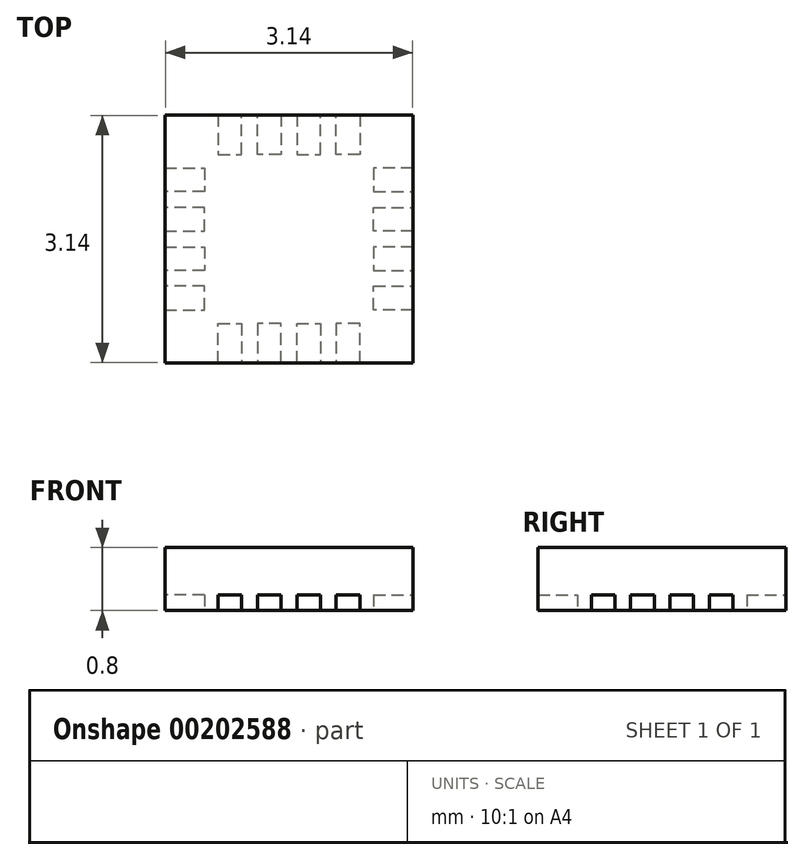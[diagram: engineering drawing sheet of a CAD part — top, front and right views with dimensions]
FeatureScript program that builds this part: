
annotation { "Feature Type Name" : "Feature", "Feature Type Description" : "" }
export const myFeature = defineFeature(function(context is Context, id is Id, definition is map)
    precondition{}
    {
        {
            var Q0;
            Q0=qCreatedBy(makeId("Top.planeOp"),FACE);
            var sketch = newSketch(context, id + "F0", { "sketchPlane" : qUnion([Q0])});
            skLineSegment(sketch, "E0.bottom", {"start": v(1.57, 1.57) * mm, "end": v(-1.58, 1.57) * mm});
            skLineSegment(sketch, "E0.top", {"start": v(1.57, -1.57) * mm, "end": v(-1.58, -1.57) * mm});
            skLineSegment(sketch, "E0.left", {"start": v(1.57, 1.58) * mm, "end": v(1.57, -1.57) * mm});
            skLineSegment(sketch, "E0.right", {"start": v(-1.58, 1.57) * mm, "end": v(-1.58, -1.57) * mm});
            skPoint(sketch, "E0.middle", {"position": v(0, 0) * mm});
            skSolve(sketch);
        }
        {
            var Q0;
            Q0 = qSketchRegion(id + "F0", true);
            extrude(context, id + "F1", {"entities" : qUnion([Q0]), "depth" : 0.8 * mm});
        }
        {
            var Q0;
            Q0=makeQuery(id+"F1.opExtrude","CAP_FACE",FACE,{"disambiguationData":[OSD([sQuery(id+"F0.wireOp",EDGE,"E0.bottom"),sQuery(id+"F0.wireOp",EDGE,"E0.top"),sQuery(id+"F0.wireOp",EDGE,"E0.left"),sQuery(id+"F0.wireOp",EDGE,"E0.right")])],"isStart":true});
            var sketch = newSketch(context, id + "F2", { "sketchPlane" : qUnion([Q0])});
            skLineSegment(sketch, "E1", {"start": v(0, 0) * mm, "end": v(0, 1.57) * mm, "construction": true});
            skPoint(sketch, "E2", {"position": v(0.25, 1.57) * mm});
            skLineSegment(sketch, "E3", {"start": v(0.1, 1.57) * mm, "end": v(0.4, 1.57) * mm});
            skLineSegment(sketch, "E4", {"start": v(0.1, 1.57) * mm, "end": v(0.1, 1.07) * mm});
            skLineSegment(sketch, "E5", {"start": v(0.1, 1.07) * mm, "end": v(0.4, 1.07) * mm});
            skLineSegment(sketch, "E6", {"start": v(0.4, 1.07) * mm, "end": v(0.4, 1.57) * mm});
            skPoint(sketch, "E7.MirrorP", {"position": v(0.75, 1.58) * mm});
            skLineSegment(sketch, "E8.MirrorCS", {"start": v(0.9, 1.58) * mm, "end": v(0.6, 1.58) * mm});
            skLineSegment(sketch, "E9.MirrorCS", {"start": v(0.9, 1.58) * mm, "end": v(0.9, 1.08) * mm});
            skLineSegment(sketch, "E10.MirrorCS", {"start": v(0.6, 1.08) * mm, "end": v(0.6, 1.58) * mm});
            skLineSegment(sketch, "E11.MirrorCS", {"start": v(0.9, 1.08) * mm, "end": v(0.6, 1.08) * mm});
            skLineSegment(sketch, "E12.MirrorCS", {"start": v(-0.1, 1.57) * mm, "end": v(-0.4, 1.57) * mm});
            skPoint(sketch, "E13.MirrorP", {"position": v(-0.25, 1.57) * mm});
            skLineSegment(sketch, "E14.MirrorCS", {"start": v(-0.1, 1.57) * mm, "end": v(-0.1, 1.07) * mm});
            skPoint(sketch, "E15.MirrorP", {"position": v(-0.75, 1.58) * mm});
            skLineSegment(sketch, "E16.MirrorCS", {"start": v(-0.1, 1.07) * mm, "end": v(-0.4, 1.07) * mm});
            skLineSegment(sketch, "E17.MirrorCS", {"start": v(-0.4, 1.07) * mm, "end": v(-0.4, 1.57) * mm});
            skLineSegment(sketch, "E18.MirrorCS", {"start": v(-0.9, 1.58) * mm, "end": v(-0.6, 1.58) * mm});
            skLineSegment(sketch, "E19.MirrorCS", {"start": v(-0.9, 1.57) * mm, "end": v(-0.9, 1.07) * mm});
            skLineSegment(sketch, "E20.MirrorCS", {"start": v(-0.6, 1.08) * mm, "end": v(-0.6, 1.58) * mm});
            skLineSegment(sketch, "E21.MirrorCS", {"start": v(-0.9, 1.08) * mm, "end": v(-0.6, 1.08) * mm});
            skPoint(sketch, "E22.1.0", {"position": v(-1.58, -0.75) * mm});
            skLineSegment(sketch, "E22.1.1", {"start": v(-1.57, 0.1) * mm, "end": v(-1.57, 0.4) * mm});
            skLineSegment(sketch, "E22.1.2", {"start": v(-1.08, 0.6) * mm, "end": v(-1.58, 0.6) * mm});
            skLineSegment(sketch, "E22.1.3", {"start": v(-1.58, -0.9) * mm, "end": v(-1.58, -0.6) * mm});
            skLineSegment(sketch, "E22.1.4", {"start": v(-1.58, 0.9) * mm, "end": v(-1.08, 0.9) * mm});
            skLineSegment(sketch, "E22.1.5", {"start": v(-1.58, 0.9) * mm, "end": v(-1.58, 0.6) * mm});
            skLineSegment(sketch, "E22.1.6", {"start": v(-1.08, 0.9) * mm, "end": v(-1.08, 0.6) * mm});
            skPoint(sketch, "E22.1.7", {"position": v(-1.58, 0.75) * mm});
            skLineSegment(sketch, "E22.1.8", {"start": v(-1.07, 0.4) * mm, "end": v(-1.57, 0.4) * mm});
            skLineSegment(sketch, "E22.1.9", {"start": v(-1.07, 0.1) * mm, "end": v(-1.07, 0.4) * mm});
            skLineSegment(sketch, "E22.1.10", {"start": v(-1.57, -0.9) * mm, "end": v(-1.07, -0.9) * mm});
            skLineSegment(sketch, "E22.1.11", {"start": v(-1.57, 0.1) * mm, "end": v(-1.07, 0.1) * mm});
            skPoint(sketch, "E22.1.12", {"position": v(-1.57, 0.25) * mm});
            skPoint(sketch, "E22.1.13", {"position": v(-1.57, -0.25) * mm});
            skLineSegment(sketch, "E22.1.14", {"start": v(-1.08, -0.9) * mm, "end": v(-1.08, -0.6) * mm});
            skLineSegment(sketch, "E22.1.15", {"start": v(-1.07, -0.4) * mm, "end": v(-1.57, -0.4) * mm});
            skLineSegment(sketch, "E22.1.16", {"start": v(-1.08, -0.6) * mm, "end": v(-1.58, -0.6) * mm});
            skLineSegment(sketch, "E22.1.17", {"start": v(-1.07, -0.1) * mm, "end": v(-1.07, -0.4) * mm});
            skLineSegment(sketch, "E22.1.18", {"start": v(-1.57, -0.1) * mm, "end": v(-1.07, -0.1) * mm});
            skLineSegment(sketch, "E22.1.19", {"start": v(-1.57, -0.1) * mm, "end": v(-1.57, -0.4) * mm});
            skPoint(sketch, "E22.2.0", {"position": v(0.75, -1.58) * mm});
            skLineSegment(sketch, "E22.2.1", {"start": v(-0.1, -1.57) * mm, "end": v(-0.4, -1.57) * mm});
            skLineSegment(sketch, "E22.2.2", {"start": v(-0.6, -1.08) * mm, "end": v(-0.6, -1.58) * mm});
            skLineSegment(sketch, "E22.2.3", {"start": v(0.9, -1.58) * mm, "end": v(0.6, -1.58) * mm});
            skLineSegment(sketch, "E22.2.4", {"start": v(-0.9, -1.57) * mm, "end": v(-0.9, -1.07) * mm});
            skLineSegment(sketch, "E22.2.5", {"start": v(-0.9, -1.58) * mm, "end": v(-0.6, -1.58) * mm});
            skLineSegment(sketch, "E22.2.6", {"start": v(-0.9, -1.08) * mm, "end": v(-0.6, -1.08) * mm});
            skPoint(sketch, "E22.2.7", {"position": v(-0.75, -1.58) * mm});
            skLineSegment(sketch, "E22.2.8", {"start": v(-0.4, -1.07) * mm, "end": v(-0.4, -1.57) * mm});
            skLineSegment(sketch, "E22.2.9", {"start": v(-0.1, -1.07) * mm, "end": v(-0.4, -1.07) * mm});
            skLineSegment(sketch, "E22.2.10", {"start": v(0.9, -1.58) * mm, "end": v(0.9, -1.08) * mm});
            skLineSegment(sketch, "E22.2.11", {"start": v(-0.1, -1.57) * mm, "end": v(-0.1, -1.07) * mm});
            skPoint(sketch, "E22.2.12", {"position": v(-0.25, -1.57) * mm});
            skPoint(sketch, "E22.2.13", {"position": v(0.25, -1.57) * mm});
            skLineSegment(sketch, "E22.2.14", {"start": v(0.9, -1.08) * mm, "end": v(0.6, -1.08) * mm});
            skLineSegment(sketch, "E22.2.15", {"start": v(0.4, -1.07) * mm, "end": v(0.4, -1.57) * mm});
            skLineSegment(sketch, "E22.2.16", {"start": v(0.6, -1.08) * mm, "end": v(0.6, -1.58) * mm});
            skLineSegment(sketch, "E22.2.17", {"start": v(0.1, -1.07) * mm, "end": v(0.4, -1.07) * mm});
            skLineSegment(sketch, "E22.2.18", {"start": v(0.1, -1.57) * mm, "end": v(0.1, -1.07) * mm});
            skLineSegment(sketch, "E22.2.19", {"start": v(0.1, -1.57) * mm, "end": v(0.4, -1.57) * mm});
            skPoint(sketch, "E22.3.0", {"position": v(1.58, 0.75) * mm});
            skLineSegment(sketch, "E22.3.1", {"start": v(1.57, -0.1) * mm, "end": v(1.57, -0.4) * mm});
            skLineSegment(sketch, "E22.3.2", {"start": v(1.07, -0.6) * mm, "end": v(1.57, -0.6) * mm});
            skLineSegment(sketch, "E22.3.3", {"start": v(1.58, 0.9) * mm, "end": v(1.58, 0.6) * mm});
            skLineSegment(sketch, "E22.3.4", {"start": v(1.57, -0.9) * mm, "end": v(1.07, -0.9) * mm});
            skLineSegment(sketch, "E22.3.5", {"start": v(1.57, -0.9) * mm, "end": v(1.57, -0.6) * mm});
            skLineSegment(sketch, "E22.3.6", {"start": v(1.07, -0.9) * mm, "end": v(1.07, -0.6) * mm});
            skPoint(sketch, "E22.3.7", {"position": v(1.57, -0.75) * mm});
            skLineSegment(sketch, "E22.3.8", {"start": v(1.07, -0.4) * mm, "end": v(1.57, -0.4) * mm});
            skLineSegment(sketch, "E22.3.9", {"start": v(1.07, -0.1) * mm, "end": v(1.07, -0.4) * mm});
            skLineSegment(sketch, "E22.3.10", {"start": v(1.58, 0.9) * mm, "end": v(1.08, 0.9) * mm});
            skLineSegment(sketch, "E22.3.11", {"start": v(1.57, -0.1) * mm, "end": v(1.07, -0.1) * mm});
            skPoint(sketch, "E22.3.12", {"position": v(1.57, -0.25) * mm});
            skPoint(sketch, "E22.3.13", {"position": v(1.57, 0.25) * mm});
            skLineSegment(sketch, "E22.3.14", {"start": v(1.08, 0.9) * mm, "end": v(1.08, 0.6) * mm});
            skLineSegment(sketch, "E22.3.15", {"start": v(1.07, 0.4) * mm, "end": v(1.57, 0.4) * mm});
            skLineSegment(sketch, "E22.3.16", {"start": v(1.08, 0.6) * mm, "end": v(1.58, 0.6) * mm});
            skLineSegment(sketch, "E22.3.17", {"start": v(1.07, 0.1) * mm, "end": v(1.07, 0.4) * mm});
            skLineSegment(sketch, "E22.3.18", {"start": v(1.57, 0.1) * mm, "end": v(1.07, 0.1) * mm});
            skLineSegment(sketch, "E22.3.19", {"start": v(1.57, 0.1) * mm, "end": v(1.57, 0.4) * mm});
            skPoint(sketch, "E22.center", {"position": v(0, 0) * mm});
            skSolve(sketch);
        }
        {
            var Q0;
            Q0 = qSketchRegion(id + "F2", true);
            extrude(context, id + "F3", {"entities" : qUnion([Q0]), "operationType" : NewBodyOperationType.REMOVE, "oppositeDirection" : true, "depth" : 0.2 * mm});
        }
        {
            var Q0;
            Q0 = qSketchRegion(id + "F2", true);
            extrude(context, id + "F4", {"entities" : qUnion([Q0]), "oppositeDirection" : true, "depth" : 0.2 * mm});
        }
    });
